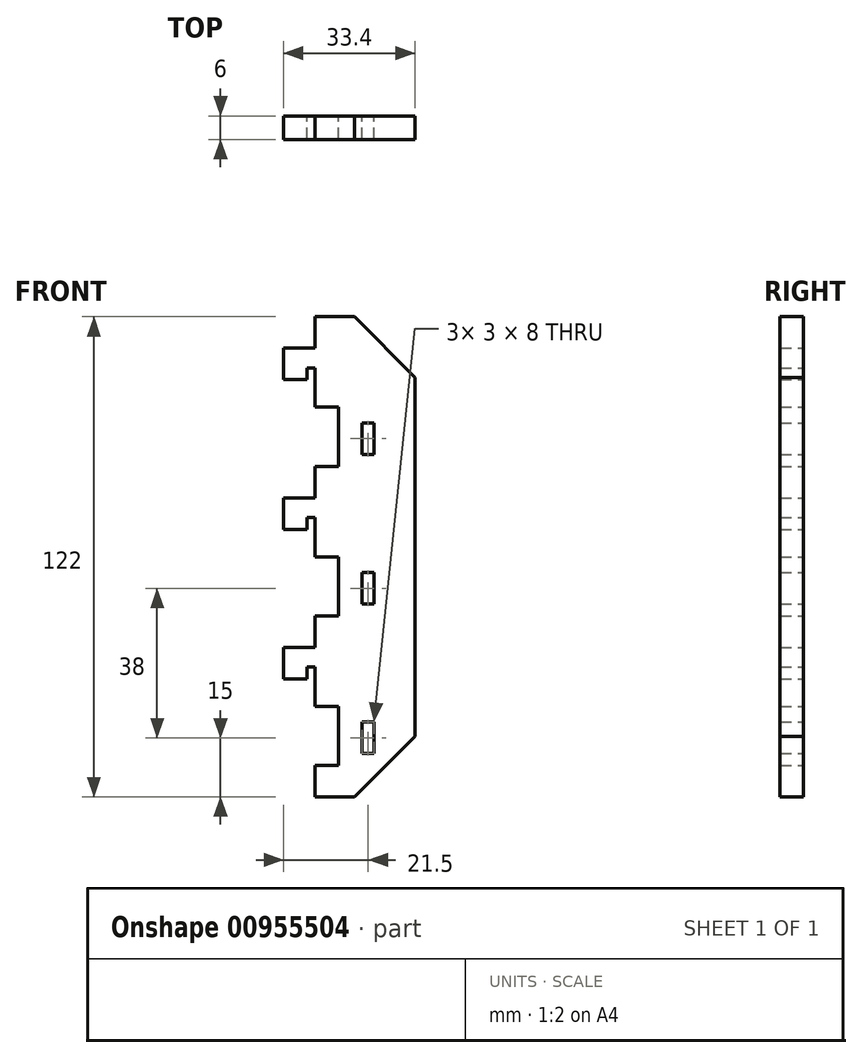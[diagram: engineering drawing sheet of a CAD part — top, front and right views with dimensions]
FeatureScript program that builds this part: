
annotation { "Feature Type Name" : "Feature", "Feature Type Description" : "" }
export const myFeature = defineFeature(function(context is Context, id is Id, definition is map)
    precondition{}
    {
        {
            var Q0;
            Q0=qCreatedBy(makeId("Front.planeOp"),FACE);
            var sketch = newSketch(context, id + "F0", { "sketchPlane" : qUnion([Q0])});
            skLineSegment(sketch, "E0", {"start": v(0, 38) * mm, "end": v(-8, 38) * mm});
            skLineSegment(sketch, "E1", {"start": v(-8, 38) * mm, "end": v(-8, 30) * mm});
            skLineSegment(sketch, "E2", {"start": v(-8, 30) * mm, "end": v(-2, 30) * mm});
            skLineSegment(sketch, "E3", {"start": v(-2, 30) * mm, "end": v(-2, 33) * mm});
            skLineSegment(sketch, "E4", {"start": v(-2, 33) * mm, "end": v(0, 33) * mm});
            skLineSegment(sketch, "E5", {"start": v(0, 33) * mm, "end": v(0, 23) * mm});
            skLineSegment(sketch, "E6.0.1.0", {"start": v(-8, 76) * mm, "end": v(-8, 68) * mm});
            skLineSegment(sketch, "E6.0.1.1", {"start": v(0, 76) * mm, "end": v(-8, 76) * mm});
            skLineSegment(sketch, "E6.0.1.2", {"start": v(-8, 68) * mm, "end": v(-2, 68) * mm});
            skLineSegment(sketch, "E6.0.1.3", {"start": v(-2, 68) * mm, "end": v(-2, 71) * mm});
            skLineSegment(sketch, "E6.0.1.4", {"start": v(-2, 71) * mm, "end": v(0, 71) * mm});
            skLineSegment(sketch, "E6.0.1.5", {"start": v(0, 71) * mm, "end": v(0, 61) * mm});
            skLineSegment(sketch, "E6.0.2.0", {"start": v(-8, 114) * mm, "end": v(-8, 106) * mm});
            skLineSegment(sketch, "E6.0.2.1", {"start": v(0, 114) * mm, "end": v(-8, 114) * mm});
            skLineSegment(sketch, "E6.0.2.2", {"start": v(-8, 106) * mm, "end": v(-2, 106) * mm});
            skLineSegment(sketch, "E6.0.2.3", {"start": v(-2, 106) * mm, "end": v(-2, 109) * mm});
            skLineSegment(sketch, "E6.0.2.4", {"start": v(-2, 109) * mm, "end": v(0, 109) * mm});
            skLineSegment(sketch, "E6.0.2.5", {"start": v(0, 109) * mm, "end": v(0, 99) * mm});
            skLineSegment(sketch, "E6.direction1", {"start": v(-8, 30) * mm, "end": v(17, 30) * mm, "construction": true});
            skLineSegment(sketch, "E6.direction2", {"start": v(-8, 30) * mm, "end": v(-8, 68) * mm, "construction": true});
            skPoint(sketch, "E7.orphan", {"position": v(0, 76) * mm});
            skLineSegment(sketch, "E8", {"start": v(0, 114) * mm, "end": v(0, 122) * mm});
            skLineSegment(sketch, "E9", {"start": v(0, 122) * mm, "end": v(10, 122) * mm});
            skLineSegment(sketch, "E10", {"start": v(10, 122) * mm, "end": v(25.4, 106.6) * mm});
            skLineSegment(sketch, "E11", {"start": v(25.4, 106.6) * mm, "end": v(25.4, 15.4) * mm});
            skLineSegment(sketch, "E12", {"start": v(25.4, 15.4) * mm, "end": v(10, 0) * mm});
            skLineSegment(sketch, "E13", {"start": v(10, 0) * mm, "end": v(0, 0) * mm});
            skLineSegment(sketch, "E14.bottom", {"start": v(0, 99) * mm, "end": v(6, 99) * mm});
            skLineSegment(sketch, "E14.top", {"start": v(0, 84) * mm, "end": v(6, 84) * mm});
            skLineSegment(sketch, "E14.right", {"start": v(6, 99) * mm, "end": v(6, 84) * mm});
            skLineSegment(sketch, "E15.trimOffspring", {"start": v(0, 84) * mm, "end": v(0, 76) * mm});
            skLineSegment(sketch, "E16.0.1.0", {"start": v(0, 61) * mm, "end": v(6, 61) * mm});
            skLineSegment(sketch, "E16.0.1.1", {"start": v(6, 61) * mm, "end": v(6, 46) * mm});
            skLineSegment(sketch, "E16.0.1.2", {"start": v(0, 46) * mm, "end": v(6, 46) * mm});
            skLineSegment(sketch, "E16.0.2.0", {"start": v(0, 23) * mm, "end": v(6, 23) * mm});
            skLineSegment(sketch, "E16.0.2.1", {"start": v(6, 23) * mm, "end": v(6, 8) * mm});
            skLineSegment(sketch, "E16.0.2.2", {"start": v(0, 8) * mm, "end": v(6, 8) * mm});
            skLineSegment(sketch, "E16.direction1", {"start": v(0, 99) * mm, "end": v(25, 99) * mm, "construction": true});
            skLineSegment(sketch, "E16.direction2", {"start": v(0, 99) * mm, "end": v(0, 61) * mm, "construction": true});
            skLineSegment(sketch, "E17.trimOffspring", {"start": v(0, 46) * mm, "end": v(0, 38) * mm});
            skLineSegment(sketch, "E18.trimOffspring", {"start": v(0, 8) * mm, "end": v(0, 0) * mm});
            skLineSegment(sketch, "E19.bottom", {"start": v(12, 95) * mm, "end": v(15, 95) * mm});
            skLineSegment(sketch, "E19.top", {"start": v(12, 87) * mm, "end": v(15, 87) * mm});
            skLineSegment(sketch, "E19.left", {"start": v(12, 95) * mm, "end": v(12, 87) * mm});
            skLineSegment(sketch, "E19.right", {"start": v(15, 95) * mm, "end": v(15, 87) * mm});
            skLineSegment(sketch, "E20.0.1.0", {"start": v(12, 57) * mm, "end": v(12, 49) * mm});
            skLineSegment(sketch, "E20.0.1.1", {"start": v(12, 57) * mm, "end": v(15, 57) * mm});
            skLineSegment(sketch, "E20.0.1.2", {"start": v(15, 57) * mm, "end": v(15, 49) * mm});
            skLineSegment(sketch, "E20.0.1.3", {"start": v(12, 49) * mm, "end": v(15, 49) * mm});
            skLineSegment(sketch, "E20.0.2.0", {"start": v(12, 19) * mm, "end": v(12, 11) * mm});
            skLineSegment(sketch, "E20.0.2.1", {"start": v(12, 19) * mm, "end": v(15, 19) * mm});
            skLineSegment(sketch, "E20.0.2.2", {"start": v(15, 19) * mm, "end": v(15, 11) * mm});
            skLineSegment(sketch, "E20.0.2.3", {"start": v(12, 11) * mm, "end": v(15, 11) * mm});
            skLineSegment(sketch, "E20.direction1", {"start": v(12, 87) * mm, "end": v(37, 87) * mm, "construction": true});
            skLineSegment(sketch, "E20.direction2", {"start": v(12, 87) * mm, "end": v(12, 49) * mm, "construction": true});
            skSolve(sketch);
        }
        {
            var Q0;
            Q0=makeQuery(id+"F0.imprint","IMPRINT",FACE,{"disambiguationData":[TD([[makeQuery(id+"F0.imprint","IMPRINT",EDGE,{"derivedFrom":sQuery(id+"F0.wireOp",EDGE,"E0")}),1.0]])]});
            extrude(context, id + "F1", {"entities" : qUnion([Q0]), "depth" : 6 * mm, "offsetDistance" : 25 * mm});
        }
    });
